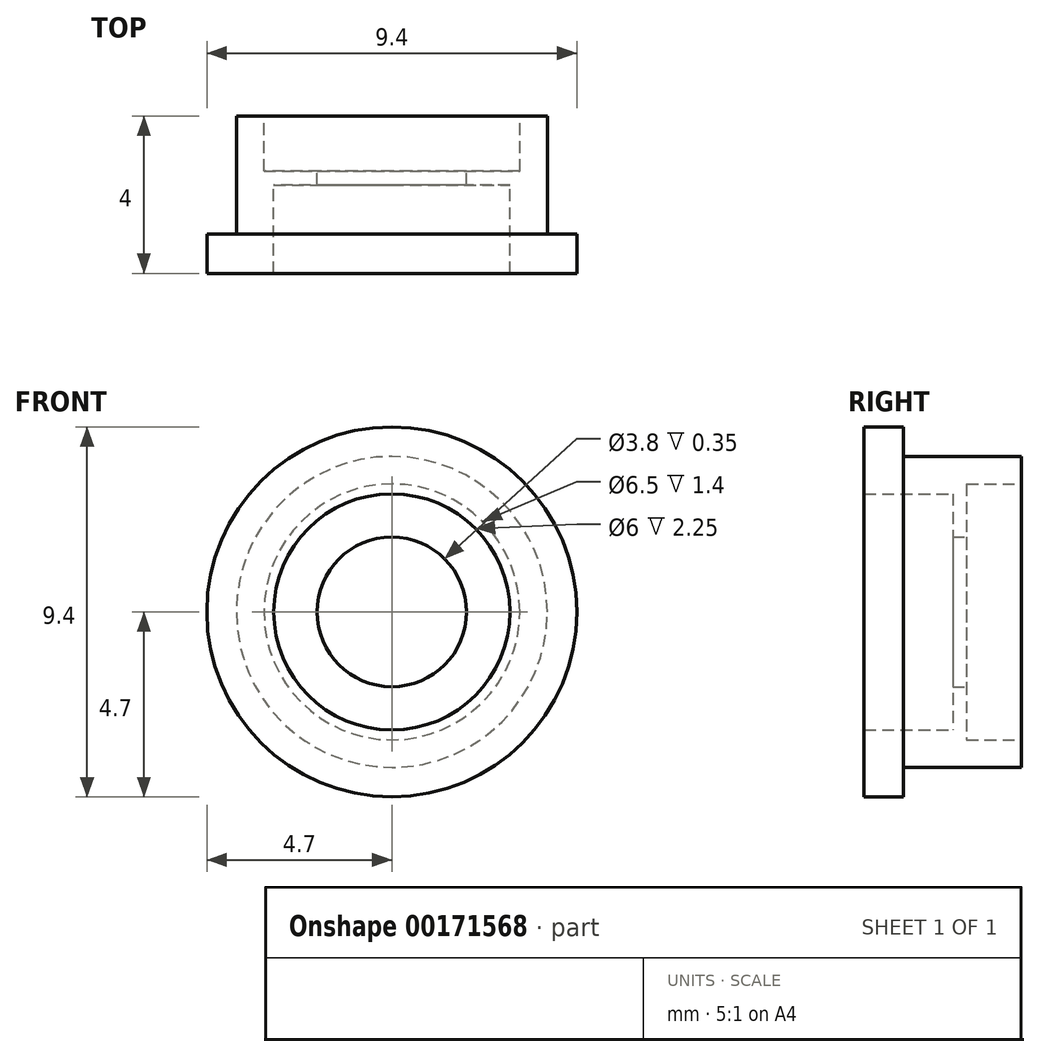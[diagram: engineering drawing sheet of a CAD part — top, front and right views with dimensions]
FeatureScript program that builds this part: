
annotation { "Feature Type Name" : "Feature", "Feature Type Description" : "" }
export const myFeature = defineFeature(function(context is Context, id is Id, definition is map)
    precondition{}
    {
        {
            var Q0;
            Q0=qCreatedBy(makeId("Right.planeOp"),FACE);
            var sketch = newSketch(context, id + "F0", { "sketchPlane" : qUnion([Q0])});
            skLineSegment(sketch, "E0", {"start": v(11.47, 0) * mm, "end": v(0, 0) * mm, "construction": true});
            skLineSegment(sketch, "E1", {"start": v(2.6, 1.9) * mm, "end": v(2.6, 3.25) * mm});
            skLineSegment(sketch, "E2", {"start": v(4, 3.25) * mm, "end": v(2.6, 3.25) * mm});
            skLineSegment(sketch, "E3", {"start": v(4, 3.25) * mm, "end": v(4, 3.95) * mm});
            skLineSegment(sketch, "E4", {"start": v(1, 3.95) * mm, "end": v(4, 3.95) * mm});
            skLineSegment(sketch, "E5", {"start": v(1, 3.95) * mm, "end": v(1, 4.7) * mm});
            skLineSegment(sketch, "E6", {"start": v(0, 4.7) * mm, "end": v(1, 4.7) * mm});
            skLineSegment(sketch, "E7", {"start": v(0, 4.7) * mm, "end": v(0, 3) * mm});
            skLineSegment(sketch, "E8", {"start": v(0, 3) * mm, "end": v(2.25, 3) * mm});
            skLineSegment(sketch, "E9", {"start": v(2.25, 3) * mm, "end": v(2.25, 1.9) * mm});
            skLineSegment(sketch, "E10", {"start": v(2.25, 1.9) * mm, "end": v(2.6, 1.9) * mm});
            skSolve(sketch);
        }
        {
            var Q0;
            Q0=makeQuery(id+"F0.imprint","IMPRINT",FACE,{"disambiguationData":[TD([[makeQuery(id+"F0.imprint","IMPRINT",EDGE,{"derivedFrom":sQuery(id+"F0.wireOp",EDGE,"E1")}),1.0]])]});
            var Q1;
            Q1=sQuery(id+"F0.wireOp",EDGE,"E0");
            revolve(context, id + "F1", {"entities" : qUnion([Q0]), "axis" : qUnion([Q1]), "revolveType" : RevolveType.FULL});
        }
    });
